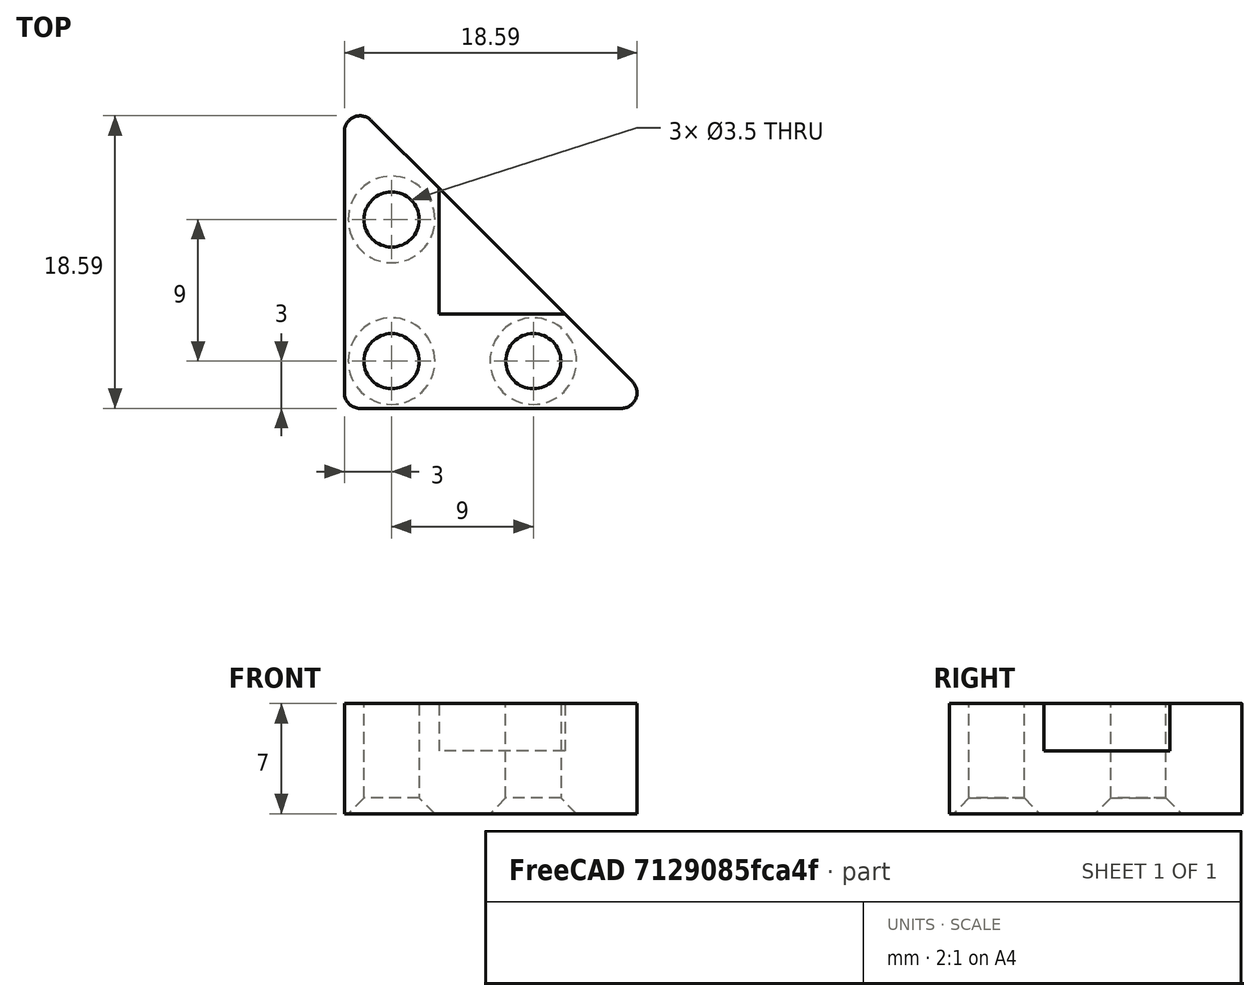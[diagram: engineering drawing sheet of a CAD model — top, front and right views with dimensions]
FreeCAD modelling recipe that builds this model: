
FCSTD DOCUMENT  (FreeCAD 0.19R24276 (Git))
Label: glass_holder
License: All rights reserved
LicenseURL: http://en.wikipedia.org/wiki/All_rights_reserved
objects: TechDraw::DrawProjGroupItem×9, TechDraw::DrawViewDimension×5, Sketcher::SketchObject×3, PartDesign::Pocket×2, PartDesign::Pad×1, PartDesign::Fillet×1, PartDesign::Chamfer×1, PartDesign::Body×1, TechDraw::DrawSVGTemplate×1, TechDraw::DrawProjGroup×1, TechDraw::DrawPage×1
note: 14 computed .brp shape members not serialized (recipe doc carries the construction recipe); baked Part::Feature solids carry a one-line shape summary decoded from their .brp

FEATURE [Sketcher::SketchObject] Sketch
  FullyConstrained = true
  MapMode = 5
  Support = -> [XY_Plane]
  sketch-geometry (3):
    g0: LineSegment StartX=0 StartY=20 StartZ=0 EndX=0 EndY=0 EndZ=0
    g1: LineSegment StartX=0 StartY=0 StartZ=0 EndX=20 EndY=0 EndZ=0
    g2: LineSegment StartX=20 StartY=0 StartZ=0 EndX=0 EndY=20 EndZ=0
  constraints (8):
    c: PointOnObject(g0,g-2)
    c: Coincident(g0,g-1)
    c: Coincident(g0,g1)
    c: PointOnObject(g1,g-1)
    c: Coincident(g1,g2)
    c: Coincident(g2,g0)
    c: DistanceX(g1,g1) = 20
    c: DistanceY(g0,g0) = 20
FEATURE [PartDesign::Pad] Pad
  Direction = (1,1,1)
  Length = 7
  Length2 = 100
  Profile = -> Sketch
  Type = 0
FEATURE [Sketcher::SketchObject] Sketch001
  ExternalGeometry = -> [Pad]
  FullyConstrained = true
  MapMode = 5
  Placement = pos=(0,0,7) rot=(0,0,1;0rad)
  Support = -> [Pad]
  sketch-geometry (3):
    g0: LineSegment StartX=6 StartY=14 StartZ=0 EndX=6 EndY=6 EndZ=0
    g1: LineSegment StartX=6 StartY=6 StartZ=0 EndX=14 EndY=6 EndZ=0
    g2: LineSegment StartX=14 StartY=6 StartZ=0 EndX=6 EndY=14 EndZ=0
  constraints (9):
    c: PointOnObject(g0,g-3)
    c: Vertical(g0)
    c: Coincident(g0,g1)
    c: PointOnObject(g1,g-3)
    c: Horizontal(g1)
    c: Coincident(g1,g2)
    c: Coincident(g2,g0)
    c: DistanceX(g-1,g0) = 6
    c: DistanceY(g-1,g0) = 6
FEATURE [PartDesign::Pocket] Pocket
  BaseFeature = -> Pad
  Length = 3
  Length2 = 100
  Profile = -> Sketch001
  Type = 0
FEATURE [Sketcher::SketchObject] Sketch002
  ExternalGeometry = -> [Pocket]
  FullyConstrained = true
  MapMode = 5
  Placement = pos=(0,0,7) rot=(0,0,1;0rad)
  Support = -> [Pocket]
  sketch-geometry (7):
    g0: LineSegment StartX=6 StartY=14 StartZ=0 EndX=0 EndY=14 EndZ=0
    g1: LineSegment StartX=14 StartY=6 StartZ=0 EndX=14 EndY=0 EndZ=0
    g2: LineSegment StartX=3 StartY=14 StartZ=0 EndX=3 EndY=0 EndZ=0
    g3: LineSegment StartX=14 StartY=3 StartZ=0 EndX=3 EndY=3 EndZ=0
    g4: Circle CenterX=3 CenterY=3 CenterZ=0 NormalX=0 NormalY=0 NormalZ=1 AngleXU=0 Radius=1.75
    g5: Circle CenterX=12 CenterY=3 CenterZ=0 NormalX=0 NormalY=0 NormalZ=1 AngleXU=0 Radius=1.75
    g6: Circle CenterX=3 CenterY=12 CenterZ=0 NormalX=0 NormalY=0 NormalZ=1 AngleXU=0 Radius=1.75
  constraints (20):
    c: Coincident(g0,g-3)
    c: PointOnObject(g0,g-4)
    c: Horizontal(g0)
    c: Coincident(g1,g-6)
    c: PointOnObject(g1,g-5)
    c: Vertical(g1)
    c: PointOnObject(g2,g-5)
    c: Vertical(g2)
    c: PointOnObject(g3,g2)
    c: Horizontal(g3)
    c: Symmetric(g0,g0,g2)
    c: Symmetric(g1,g1,g3)
    c: Coincident(g4,g3)
    c: PointOnObject(g5,g3)
    c: PointOnObject(g6,g2)
    c: Radius(g6) = 1.75
    c: Equal(g6,g4)
    c: Equal(g6,g5)
    c: DistanceX(g4,g5) = 9
    c: DistanceY(g4,g6) = 9
FEATURE [PartDesign::Pocket] Pocket001
  BaseFeature = -> Pocket
  Length = 5
  Length2 = 100
  Profile = -> Sketch002
  Type = 1
FEATURE [PartDesign::Fillet] Fillet
  Base = -> Pocket001 [Edge2,Edge11,Edge1]
  BaseFeature = -> Pocket001
  Radius = 1
  SupportTransform = false
FEATURE [PartDesign::Chamfer] Chamfer
  Angle = 45
  Base = -> Fillet [Edge12,Edge11,Edge10]
  BaseFeature = -> Fillet
  ChamferType = 0
  FlipDirection = false
  Size = 1
  Size2 = 1
  SupportTransform = false
FEATURE [PartDesign::Body] Body
  Group = -> [Sketch,Pad,Sketch001,Pocket,Sketch002,Pocket001,Fillet,Chamfer]
  Origin = -> Origin
  Tip = -> Chamfer
FEATURE [TechDraw::DrawSVGTemplate] Template_Chamfer
  Height = 210
  Orientation = 1
  Width = 297
FEATURE [TechDraw::DrawProjGroupItem] ProjItem  label="Front"
  CoarseView = false
  Direction = (0,-1,0)
  Focus = 100
  HardHidden = false
  IsoCount = 0
  IsoHidden = false
  IsoVisible = false
  LockPosition = true
  Perspective = false
  Rotation = 0
  RotationVector = (1,0,0)
  ScaleType = 2
  SeamHidden = false
  SeamVisible = true
  SmoothHidden = false
  SmoothVisible = true
  Source = -> [Chamfer]
  Type = 0
  X = 0
  XDirection = (1,0,0)
  Y = 0
FEATURE [TechDraw::DrawProjGroupItem] ProjItem001  label="Right"
  CoarseView = false
  Direction = (1,-1e-16,0)
  Focus = 100
  HardHidden = false
  IsoCount = 0
  IsoHidden = false
  IsoVisible = false
  LockPosition = false
  Perspective = false
  Rotation = 0
  RotationVector = (1,0,0)
  ScaleType = 2
  SeamHidden = false
  SeamVisible = true
  SmoothHidden = false
  SmoothVisible = true
  Source = -> [Chamfer]
  Type = 2
  X = -37.0208
  XDirection = (1e-16,1,0)
  Y = 0
FEATURE [TechDraw::DrawProjGroupItem] ProjItem002  label="Top"
  CoarseView = false
  Direction = (0,0,1)
  Focus = 100
  HardHidden = false
  IsoCount = 0
  IsoHidden = false
  IsoVisible = false
  LockPosition = false
  Perspective = false
  Rotation = 0
  RotationVector = (1,0,0)
  ScaleType = 2
  SeamHidden = false
  SeamVisible = true
  SmoothHidden = false
  SmoothVisible = true
  Source = -> [Chamfer]
  Type = 4
  X = 0
  XDirection = (1,0,0)
  Y = -43.8909
FEATURE [TechDraw::DrawProjGroupItem] ProjItem003  label="Left"
  CoarseView = false
  Direction = (-1,-1e-16,0)
  Focus = 100
  HardHidden = false
  IsoCount = 0
  IsoHidden = false
  IsoVisible = false
  LockPosition = false
  Perspective = false
  Rotation = 0
  RotationVector = (1,0,0)
  ScaleType = 2
  SeamHidden = false
  SeamVisible = true
  SmoothHidden = false
  SmoothVisible = true
  Source = -> [Chamfer]
  Type = 1
  X = 37.0208
  XDirection = (1e-16,-1,0)
  Y = 0
FEATURE [TechDraw::DrawProjGroupItem] ProjItem004  label="Bottom"
  CoarseView = false
  Direction = (0,0,-1)
  Focus = 100
  HardHidden = false
  IsoCount = 0
  IsoHidden = false
  IsoVisible = false
  LockPosition = false
  Perspective = false
  Rotation = 0
  RotationVector = (1,0,0)
  ScaleType = 2
  SeamHidden = false
  SeamVisible = true
  SmoothHidden = false
  SmoothVisible = true
  Source = -> [Chamfer]
  Type = 5
  X = 0
  XDirection = (1,0,0)
  Y = 37.0208
FEATURE [TechDraw::DrawProjGroupItem] ProjItem005  label="FrontBottomLeft"
  CoarseView = false
  Direction = (-0.57735,-0.57735,-0.57735)
  Focus = 100
  HardHidden = false
  IsoCount = 0
  IsoHidden = false
  IsoVisible = false
  LockPosition = false
  Perspective = false
  Rotation = 0
  RotationVector = (1,0,0)
  ScaleType = 2
  SeamHidden = false
  SeamVisible = true
  SmoothHidden = false
  SmoothVisible = true
  Source = -> [Chamfer]
  Type = 8
  X = 40.4558
  XDirection = (0.707107,-0.707107,0)
  Y = 34.5486
FEATURE [TechDraw::DrawProjGroupItem] ProjItem006  label="FrontTopRight"
  CoarseView = false
  Direction = (0.57735,-0.57735,0.57735)
  Focus = 100
  HardHidden = false
  IsoCount = 0
  IsoHidden = false
  IsoVisible = false
  LockPosition = false
  Perspective = false
  Rotation = 0
  RotationVector = (1,0,0)
  ScaleType = 2
  SeamHidden = false
  SeamVisible = true
  SmoothHidden = false
  SmoothVisible = true
  Source = -> [Chamfer]
  Type = 7
  X = -34.5919
  XDirection = (0.707107,0.707107,0)
  Y = -42.9776
FEATURE [TechDraw::DrawProjGroupItem] ProjItem007  label="FrontTopLeft"
  CoarseView = false
  Direction = (-0.57735,-0.57735,0.57735)
  Focus = 100
  HardHidden = false
  IsoCount = 0
  IsoHidden = false
  IsoVisible = false
  LockPosition = false
  Perspective = false
  Rotation = 0
  RotationVector = (1,0,0)
  ScaleType = 2
  SeamHidden = false
  SeamVisible = true
  SmoothHidden = false
  SmoothVisible = true
  Source = -> [Chamfer]
  Type = 6
  X = 40.4558
  XDirection = (0.707107,-0.707107,0)
  Y = -46.3631
FEATURE [TechDraw::DrawProjGroupItem] ProjItem008  label="FrontBottomRight"
  CoarseView = false
  Direction = (0.57735,-0.57735,-0.57735)
  Focus = 100
  HardHidden = false
  IsoCount = 0
  IsoHidden = false
  IsoVisible = false
  LockPosition = false
  Perspective = false
  Rotation = 0
  RotationVector = (1,0,0)
  ScaleType = 2
  SeamHidden = false
  SeamVisible = true
  SmoothHidden = false
  SmoothVisible = true
  Source = -> [Chamfer]
  Type = 9
  X = -34.5919
  XDirection = (0.707107,0.707107,0)
  Y = 37.9341
FEATURE [TechDraw::DrawProjGroup] ProjGroup_Chamfer
  Anchor = -> ProjItem
  AutoDistribute = true
  LockPosition = false
  ProjectionType = 0
  Rotation = 0
  ScaleType = 1
  Source = -> [Chamfer]
  Views = -> [ProjItem,ProjItem001,ProjItem002,ProjItem003,ProjItem004,ProjItem005,ProjItem006,ProjItem007,ProjItem008]
  X = 148.5
  Y = 105
  spacingX = 15
  spacingY = 15
FEATURE [TechDraw::DrawViewDimension] Dimension
  Arbitrary = false
  ArbitraryTolerances = false
  EqualTolerance = true
  FormatSpec = %.2f
  FormatSpecOverTolerance = %+.2f
  FormatSpecUnderTolerance = %+.2f
  Inverted = false
  LockPosition = false
  MeasureType = 1
  OverTolerance = 0
  References2D = -> [ProjItem]
  Rotation = 0
  ScaleType = 0
  TheoreticalExact = false
  Type = 2
  UnderTolerance = 0
  X = -19.0569
  Y = 0.168345
FEATURE [TechDraw::DrawViewDimension] Dimension001
  Arbitrary = false
  ArbitraryTolerances = false
  EqualTolerance = true
  FormatSpec = R%.2f
  FormatSpecOverTolerance = %+.2f
  FormatSpecUnderTolerance = %+.2f
  Inverted = false
  LockPosition = false
  MeasureType = 1
  OverTolerance = 0
  References2D = -> [ProjItem004]
  Rotation = 0
  ScaleType = 0
  TheoreticalExact = false
  Type = 4
  UnderTolerance = 0
  X = 20.6029
  Y = 14.3035
FEATURE [TechDraw::DrawViewDimension] Dimension002
  Arbitrary = false
  ArbitraryTolerances = false
  EqualTolerance = true
  FormatSpec = %.2f
  FormatSpecOverTolerance = %+.2f
  FormatSpecUnderTolerance = %+.2f
  Inverted = false
  LockPosition = false
  MeasureType = 1
  OverTolerance = 0
  References2D = -> [ProjItem004]
  Rotation = 0
  ScaleType = 0
  TheoreticalExact = false
  Type = 1
  UnderTolerance = 0
  X = -1.40811
  Y = 19.0015
FEATURE [TechDraw::DrawViewDimension] Dimension003
  Arbitrary = false
  ArbitraryTolerances = false
  EqualTolerance = true
  FormatSpec = %.2f
  FormatSpecOverTolerance = %+.2f
  FormatSpecUnderTolerance = %+.2f
  Inverted = false
  LockPosition = false
  MeasureType = 1
  OverTolerance = 0
  References2D = -> [ProjItem002]
  Rotation = 0
  ScaleType = 0
  TheoreticalExact = false
  Type = 1
  UnderTolerance = 0
  X = 10.3478
  Y = 23.9942
FEATURE [TechDraw::DrawViewDimension] Dimension004
  Arbitrary = false
  ArbitraryTolerances = false
  EqualTolerance = true
  FormatSpec = ⌀%.2f
  FormatSpecOverTolerance = %+.2f
  FormatSpecUnderTolerance = %+.2f
  Inverted = false
  LockPosition = false
  MeasureType = 1
  OverTolerance = 0
  References2D = -> [ProjItem002]
  Rotation = 0
  ScaleType = 0
  TheoreticalExact = false
  Type = 5
  UnderTolerance = 0
  X = 16.7491
  Y = 7.33701
FEATURE [TechDraw::DrawPage] Page_Chamfer
  KeepUpdated = true
  NextBalloonIndex = 1
  ProjectionType = 0
  Template = -> Template_Chamfer
  Views = -> [ProjGroup_Chamfer,Dimension,Dimension001,Dimension002,Dimension003,Dimension004]
